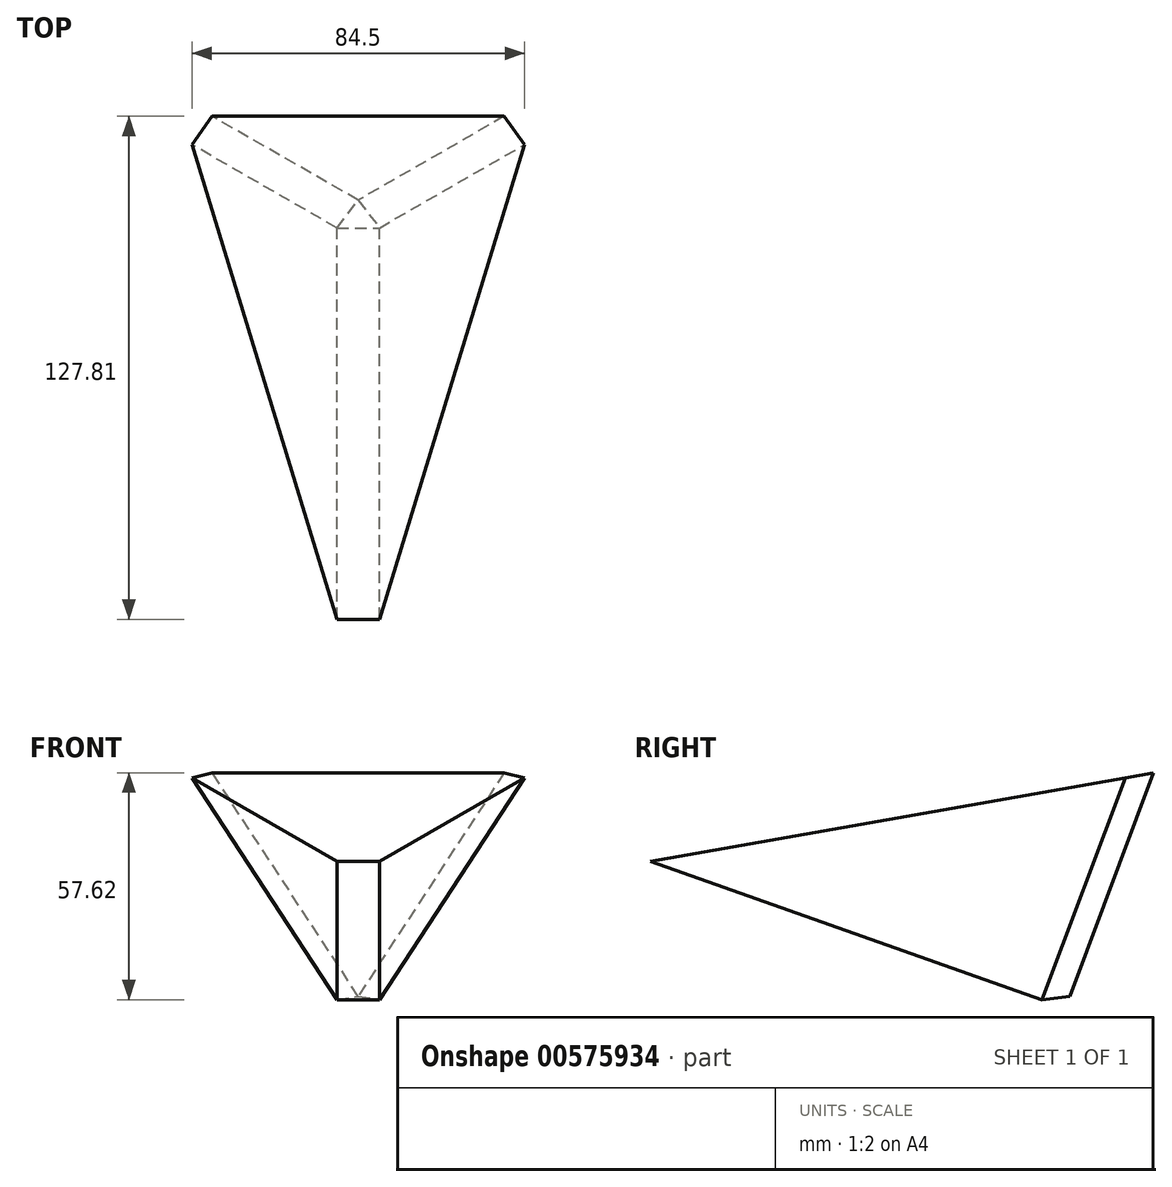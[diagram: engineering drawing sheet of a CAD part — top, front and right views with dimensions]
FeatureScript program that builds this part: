
annotation { "Feature Type Name" : "Feature", "Feature Type Description" : "" }
export const myFeature = defineFeature(function(context is Context, id is Id, definition is map)
    precondition{}
    {
        {
            var Q0;
            Q0=qCreatedBy(makeId("Front.planeOp"),FACE);
            var sketch = newSketch(context, id + "F0", { "sketchPlane" : qUnion([Q0])});
            skLineSegment(sketch, "E0", {"start": v(0, 0) * mm, "end": v(44.45, 0) * mm});
            skLineSegment(sketch, "E1", {"start": v(-44.45, 0) * mm, "end": v(0, 0) * mm});
            skLineSegment(sketch, "E2", {"start": v(44.45, 0) * mm, "end": v(22.22, -38.5) * mm});
            skLineSegment(sketch, "E3", {"start": v(22.23, -38.5) * mm, "end": v(0, -76.99) * mm});
            skLineSegment(sketch, "E4", {"start": v(-44.45, 0) * mm, "end": v(-22.22, -38.5) * mm});
            skLineSegment(sketch, "E5", {"start": v(-22.23, -38.5) * mm, "end": v(0, -76.99) * mm});
            skSolve(sketch);
        }
        {
            var Q0;
            Q0=qSketchRegion(id+"F0",true);
            extrude(context, id + "F1", {"entities" : qUnion([Q0]), "depth" : 152.15 * mm, "offsetDistance" : 25.4 * mm, "hasDraft" : true, "draftAngle" : 10 * degree, "draftPullDirection" : true});
        }
        {
            var Q0;
            Q0=qCreatedBy(makeId("Right.planeOp"),FACE);
            var sketch = newSketch(context, id + "F2", { "sketchPlane" : qUnion([Q0])});
            skLineSegment(sketch, "E6", {"start": v(0, 0) * mm, "end": v(-33.8, -90.07) * mm});
            skLineSegment(sketch, "E7", {"start": v(-33.8, -90.07) * mm, "end": v(49.3, -90.07) * mm});
            skLineSegment(sketch, "E8", {"start": v(49.3, -90.07) * mm, "end": v(0, 0) * mm});
            skSolve(sketch);
        }
        {
            var Q0;
            Q0=qSketchRegion(id+"F2",true);
            extrude(context, id + "F3", {"entities" : qUnion([Q0]), "operationType" : NewBodyOperationType.REMOVE, "endBound" : BoundingType.THROUGH_ALL, "oppositeDirection" : true, "depth" : 25.4 * mm, "offsetDistance" : 25.4 * mm});
        }
        {
            var Q0;
            Q0=makeQuery(id+"F3.boolean.opBoolean","COPY",FACE,{"derivedFrom":makeQuery(id+"F3.opExtrude","CAP_FACE",FACE,{"disambiguationData":[OSD([sQuery(id+"F2.wireOp",EDGE,"E6"),sQuery(id+"F2.wireOp",EDGE,"E7"),sQuery(id+"F2.wireOp",EDGE,"E8")])],"isStart":true})});
            extrude(context, id + "F4", {"entities" : qUnion([Q0]), "operationType" : NewBodyOperationType.REMOVE, "endBound" : BoundingType.THROUGH_ALL, "oppositeDirection" : true, "depth" : 25.4 * mm, "offsetDistance" : 25.4 * mm});
        }
        {
            var Q0;
            Q0=makeQuery(id+"F3.boolean.opBoolean","INTERSECT",EDGE,{"derivedFrom":[makeQuery(id+"F1.opExtrude","SWEPT_FACE",FACE,{"disambiguationData":[OSD([sQuery(id+"F0.wireOp",EDGE,"E4"),sQuery(id+"F0.wireOp",EDGE,"E5")])]}),makeQuery(id+"F3.opExtrude","SWEPT_FACE",FACE,{"disambiguationData":[OSD([sQuery(id+"F2.wireOp",EDGE,"E6")])]})]});
            var Q1;
            {var subQ0=sQuery(id+"F0.wireOp",EDGE,"E3");var subQ1=sQuery(id+"F0.wireOp",EDGE,"E5");Q1=makeQuery(id+"F3.boolean.opBoolean","SPLIT",EDGE,{"disambiguationData":[topologyDisambiguationEdgeConnected([makeQuery(id+"F1.opExtrude","SWEPT_FACE",FACE,{"disambiguationData":[OSD([sQuery(id+"F0.wireOp",EDGE,"E4"),subQ1])]})])],"derivedFrom":makeQuery(id+"F1.opExtrude","SWEPT_EDGE",EDGE,{"disambiguationData":[OSD([subQ0,subQ1])]})});}
            var Q2;
            Q2=makeQuery(id+"F4.boolean.opBoolean","INTERSECT",EDGE,{"derivedFrom":[makeQuery(id+"F1.opExtrude","SWEPT_FACE",FACE,{"disambiguationData":[OSD([sQuery(id+"F0.wireOp",EDGE,"E2"),sQuery(id+"F0.wireOp",EDGE,"E3")])]}),makeQuery(id+"F4.opExtrude","SWEPT_FACE",FACE,{"disambiguationData":[OSD([sQuery(id+"F2.wireOp",EDGE,"E6")])]})]});
            chamfer(context, id + "F5", {"entities" : qUnion([Q0, Q1, Q2]), "width" : 6.35 * mm, "tangentPropagation" : true});
        }
    });
